# Revit family: Bathtub-Stationary_Whirlpool-Whitehall-E-22-S-Series
name_source: partatom
category: Plumbing Fixtures
units: mm (PartAtom-declared; Revit-internal decimal feet)

## family parameters
Cut with Voids When Loaded = No
Host = Face
OmniClass Number = 23.45.05.14.21.17
OmniClass Title = Therapeutic Whirlpool Baths
Part Type = Normal
Room Calculation Point = No
Round Connector Dimension = Use Diameter
Shared = Yes

## types (3) — shared parameters
115VAC = Yes
22 22 Gallons = Yes
230VAC = No
AHC1  Adjustable High Chair with Casters = No
AHC2  Adjustable High Chair with Rubber Tips = No
ALC  Adjustable Low Chair = No
ALS  Adjustable Low Stool = No
ARS  Arm Rest Support = No
Assembly Code = D2010510
CW Connection = Yes
CWFU = 3
Default Elevation = 0"
Description = E-22-S 22 Gallon Stationary Whirlpool
E   Extremity Series = Yes
Electrical Requirement = Amps:6.9/6.2  Hertz:50/60  Volts:115  GFI Receptable
Finish - Mobile Turbine = Plastic-Whitehall-Plastic Greyish
GAL. TO OVERFLOW = 22 Gallon
GFI Ground Fault Interrupter = No
HW Connection = Yes
HWFU = 3
Height = 24"
IAPMO Compliance = Certified per US & Canadian Medical Standards; UL 60601-1 & CSA C22.2 No. 601.1
Installation Type = Floor Mount
Length = 28"
Manufacturer = Whitehall
PCS   Pump Strainer Cover = No
Price = Prices may vary. Please consult Manufacturer Representative for most up-to-date price list.
Product Documentation Link = https://www.whitehallmfg.com
Product Page URL = https://whitehallrehabilitation.com
S Stationary Whirlpool = Yes
SDO Separate Drain and Overflow Assembly = No
URL = https://whitehallrehabilitation.com
Vent Connection = No
WFU = 4
Waste Connection = Yes
Waste Connection Diameter = 2"
Waste Connection Radius = 1"
Width = 15"

## per-type parameters (varying)
| type | EG Enviro Glaze Color Powder Coating Specify Color | Finish | Material |
| E-22-S | No | Stainless Steel-Whitehall-Satin Finish | Stainless Steel-Whitehall-Satin Finish |
| E-22-S-EG07 | Yes | Stainless Steel-Whitehall-EG07-Black Color Enviro Glaze | Stainless Steel-Whitehall-EG07-Black Color Enviro Glaze |
| E-22-S-EG10 | Yes | Stainless Steel-Whitehall-EG10-White Enviro Glaze | Stainless Steel-Whitehall-EG10-White Enviro Glaze |

note: column(s) folded — value = type name in every type: Model

## geometry (parser evidence)
native form markers: Sweep x2
no freeform markers — native parametric forms only
